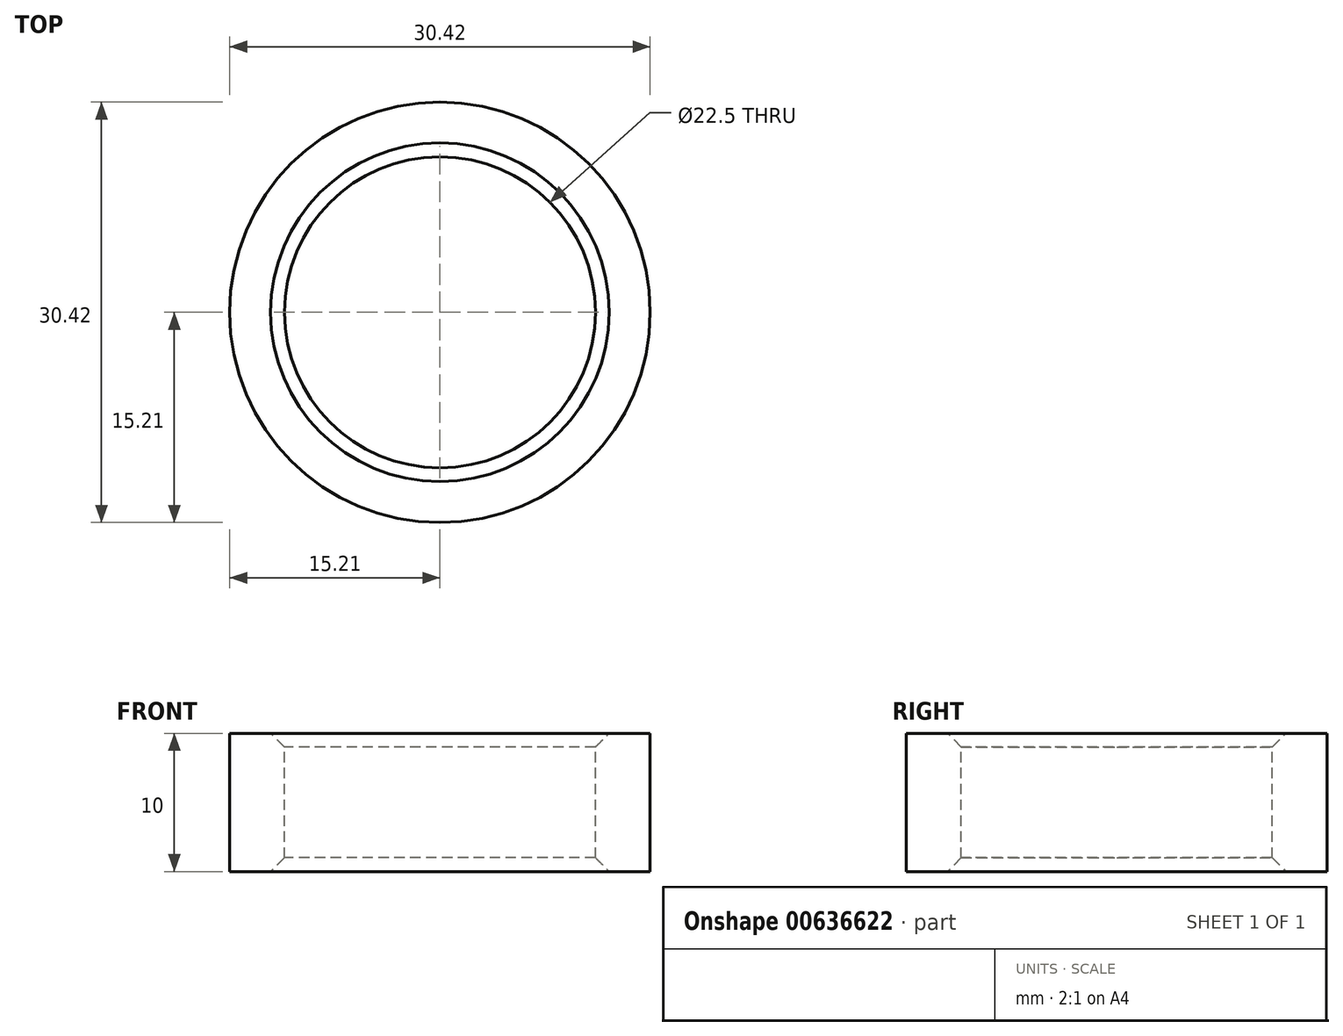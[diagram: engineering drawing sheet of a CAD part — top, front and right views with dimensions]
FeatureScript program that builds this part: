
annotation { "Feature Type Name" : "Feature", "Feature Type Description" : "" }
export const myFeature = defineFeature(function(context is Context, id is Id, definition is map)
    precondition{}
    {
        {
            var Q0;
            Q0=qCreatedBy(makeId("Top.planeOp"),FACE);
            var sketch = newSketch(context, id + "F0", { "sketchPlane" : qUnion([Q0])});
            skCircle(sketch, "E0", {"center": v(0, 0) * mm, "radius": 11.25 * mm});
            skCircle(sketch, "E1", {"center": v(0, 0) * mm, "radius": 11.75 * mm});
            skSolve(sketch);
        }
        {
            var Q0;
            Q0=makeQuery(id+"F0.imprint","IMPRINT",FACE,{"disambiguationData":[TD([[makeQuery(id+"F0.imprint","IMPRINT",EDGE,{"derivedFrom":sQuery(id+"F0.wireOp",EDGE,"E0")}),-1.0]])]});
            extrude(context, id + "F1", {"entities" : qUnion([Q0]), "oppositeDirection" : true, "depth" : 10 * mm, "offsetDistance" : 25 * mm});
        }
        {
            var Q0;
            Q0=qCreatedBy(makeId("Top.planeOp"),FACE);
            var sketch = newSketch(context, id + "F2", { "sketchPlane" : qUnion([Q0])});
            skCircle(sketch, "E2", {"center": v(0, 0) * mm, "radius": 15.21 * mm});
            skCircle(sketch, "E3", {"center": v(0, 0) * mm, "radius": 11.75 * mm});
            skSolve(sketch);
        }
        {
            var Q0;
            Q0=makeQuery(id+"F2.imprint","IMPRINT",FACE,{"disambiguationData":[TD([[makeQuery(id+"F2.imprint","IMPRINT",EDGE,{"derivedFrom":sQuery(id+"F2.wireOp",EDGE,"E2")}),1.0]])]});
            extrude(context, id + "F3", {"entities" : qUnion([Q0]), "operationType" : NewBodyOperationType.ADD, "oppositeDirection" : true, "depth" : 10 * mm, "offsetDistance" : 25 * mm});
        }
        {
            var Q0;
            Q0=makeQuery(id+"F1.opExtrude","CAP_EDGE",EDGE,{"disambiguationData":[OSD([sQuery(id+"F0.wireOp",EDGE,"E0")])],"isStart":true});
            chamfer(context, id + "F4", {"entities" : qUnion([Q0]), "width" : 1 * mm, "tangentPropagation" : true});
        }
        {
            var Q0;
            Q0=makeQuery(id+"F1.opExtrude","CAP_EDGE",EDGE,{"disambiguationData":[OSD([sQuery(id+"F0.wireOp",EDGE,"E0")])],"isStart":false});
            chamfer(context, id + "F5", {"entities" : qUnion([Q0]), "width" : 1 * mm, "tangentPropagation" : true});
        }
    });
